FCSTD DOCUMENT  (FreeCAD 0.19R24267 +99 (Git))
Label: Carro
License: All rights reserved
LicenseURL: http://en.wikipedia.org/wiki/All_rights_reserved
objects: App::DocumentObjectGroup×3, PartDesign::CoordinateSystem×1, App::FeaturePython×1, App::Link×1, App::Part×1
note: 1 computed .brp shape members not serialized (recipe doc carries the construction recipe); baked Part::Feature solids carry a one-line shape summary decoded from their .brp
EXTERNAL_REF file=Tubolare60x40-base.FCStd obj=Body

FEATURE [App::DocumentObjectGroup] Parts
FEATURE [PartDesign::CoordinateSystem] LCS_Origin
  AttacherType = Attacher::AttachEngine3D
  MapMode = 2
  Support = -> [X_Axis]
FEATURE [App::DocumentObjectGroup] Constraints
FEATURE [App::FeaturePython] Variables  # WARN: FeaturePython — macro-defined, semantics opaque (R4)
  Type = App::PropertyContainer
FEATURE [App::DocumentObjectGroup] Configurations
FEATURE [App::Link] link_Tubolare60x40  label="link-Tubolare60x40"
  LinkedObject = -> <external Tubolare60x40-base.FCStd>#Body
FEATURE [App::Part] Assembly
  AssemblyType = Part::Link
  Group = -> [LCS_Origin,Constraints,Variables,Configurations,link_Tubolare60x40]
  Origin = -> Origin
  Type = Assembly

RESOLVED EXTERNAL PARTS (link-assembly join: the EXTERNAL_REF files above that resolve inside this repo's crawl, each included once):
---- part Tubolare60x40-base.FCStd = doc fcstd_5f6e31bec396 ----
FCSTD DOCUMENT  (FreeCAD 0.21R33771 (Git))
Label: Tubolare60x40-base
License: All rights reserved
LicenseURL: http://en.wikipedia.org/wiki/All_rights_reserved
objects: Sketcher::SketchObject×1, PartDesign::Pad×1, PartDesign::CoordinateSystem×1, PartDesign::Body×1
note: 5 computed .brp shape members not serialized (recipe doc carries the construction recipe); baked Part::Feature solids carry a one-line shape summary decoded from their .brp

FEATURE [Sketcher::SketchObject] Sketch
  FullyConstrained = true
  MapMode = 5
  Support = -> [XY_Plane]
  sketch-geometry (17):
    g0: LineSegment StartX=0 StartY=0 StartZ=0 EndX=40 EndY=0 EndZ=0
    g1: LineSegment StartX=40 StartY=0 StartZ=0 EndX=40 EndY=60 EndZ=0
    g2: LineSegment StartX=40 StartY=60 StartZ=0 EndX=-15 EndY=60 EndZ=0
    g3: LineSegment StartX=0 StartY=30 StartZ=0 EndX=0 EndY=0 EndZ=0
    g4: LineSegment StartX=3 StartY=57 StartZ=0 EndX=37 EndY=57 EndZ=0
    g5: LineSegment StartX=37 StartY=57 StartZ=0 EndX=37 EndY=3 EndZ=0
    g6: LineSegment StartX=37 StartY=3 StartZ=0 EndX=3 EndY=3 EndZ=0
    g7: LineSegment StartX=3 StartY=3 StartZ=0 EndX=3 EndY=57 EndZ=0
    g8: LineSegment StartX=-40 StartY=60 StartZ=0 EndX=-40 EndY=57 EndZ=0
    g9: LineSegment StartX=-40 StartY=57 StartZ=0 EndX=-18 EndY=57 EndZ=0
    g10: LineSegment StartX=-13 StartY=52 StartZ=0 EndX=-13 EndY=30 EndZ=0
    g11: LineSegment StartX=-13 StartY=30 StartZ=0 EndX=0 EndY=30 EndZ=0
    g12: ArcOfCircle CenterX=-18 CenterY=52 CenterZ=0 NormalX=0 NormalY=0 NormalZ=1 AngleXU=0 Radius=5 StartAngle=-5.3e-15 EndAngle=1.5708
    g13: LineSegment StartX=-35 StartY=60 StartZ=0 EndX=-35 EndY=75.5 EndZ=0
    g14: LineSegment StartX=-35 StartY=75.5 StartZ=0 EndX=-15 EndY=75.5 EndZ=0
    g15: LineSegment StartX=-15 StartY=75.5 StartZ=0 EndX=-15 EndY=60 EndZ=0
    g16: LineSegment StartX=-35 StartY=60 StartZ=0 EndX=-40 EndY=60 EndZ=0
  constraints (48):
    c: Coincident(g0,g1)
    c: Coincident(g1,g2)
    c: Coincident(g3,g0)
    c: Horizontal(g0)
    c: Horizontal(g2)
    c: Vertical(g1)
    c: Vertical(g3)
    c: Coincident(g0,g-1)
    c: DistanceX(g0,g0) = 40
    c: DistanceY(g1,g1) = 60
    c: Coincident(g4,g5)
    c: Coincident(g5,g6)
    c: Coincident(g6,g7)
    c: Coincident(g7,g4)
    c: Horizontal(g4)
    c: Horizontal(g6)
    c: Vertical(g5)
    c: Vertical(g7)
    c: DistanceX(g6,g6) = 34
    c: DistanceY(g5,g5) = 54
    c: DistanceX(g0,g6) = 3
    c: DistanceY(g0,g6) = 3
    c: Vertical(g8)
    c: Coincident(g9,g8)
    c: Horizontal(g9)
    c: Vertical(g10)
    c: Coincident(g11,g10)
    c: Horizontal(g11)
    c: Coincident(g3,g11)
    c: Coincident(g16,g8)
    c: DistanceX(g16,g2) = 80
    c: DistanceY(g8,g8) = 3
    c: Tangent(g10,g12) = 1.5708
    c: Tangent(g9,g12) = 1.5708
    c: Radius(g12) = 5
    c: DistanceX(g9,g9) = 22
    c: DistanceY(g10,g10) = 22
    c: Vertical(g13)
    c: Horizontal(g14)
    c: Coincident(g15,g14)
    c: Vertical(g15)
    c: Coincident(g13,g14)
    c: Coincident(g2,g15)
    c: Coincident(g16,g13)
    c: Tangent(g2,g16)
    c: DistanceX(g14,g14) = 20
    c: DistanceX(g16,g16) = 5
    c: DistanceY(g15,g15) = 15.5
FEATURE [PartDesign::Pad] Pad
  Direction = (0,0,1)
  Length = 900
  Length2 = 100
  Profile = -> Sketch
  ReferenceAxis = -> Sketch [N_Axis]
  Type = 0
FEATURE [PartDesign::CoordinateSystem] LCS_1
  AttacherType = Attacher::AttachEngine3D
  AttachmentOffset = pos=(0,-2,0) rot=(0,0,1;0rad)
  MapMode = 7
  Placement = pos=(40,-4e-16,-2) rot=(1,0,0;1.5708rad)
  Support = -> [Pad]
FEATURE [PartDesign::Body] Body
  Group = -> [Sketch,Pad,LCS_1]
  Origin = -> Origin
  Tip = -> Pad
